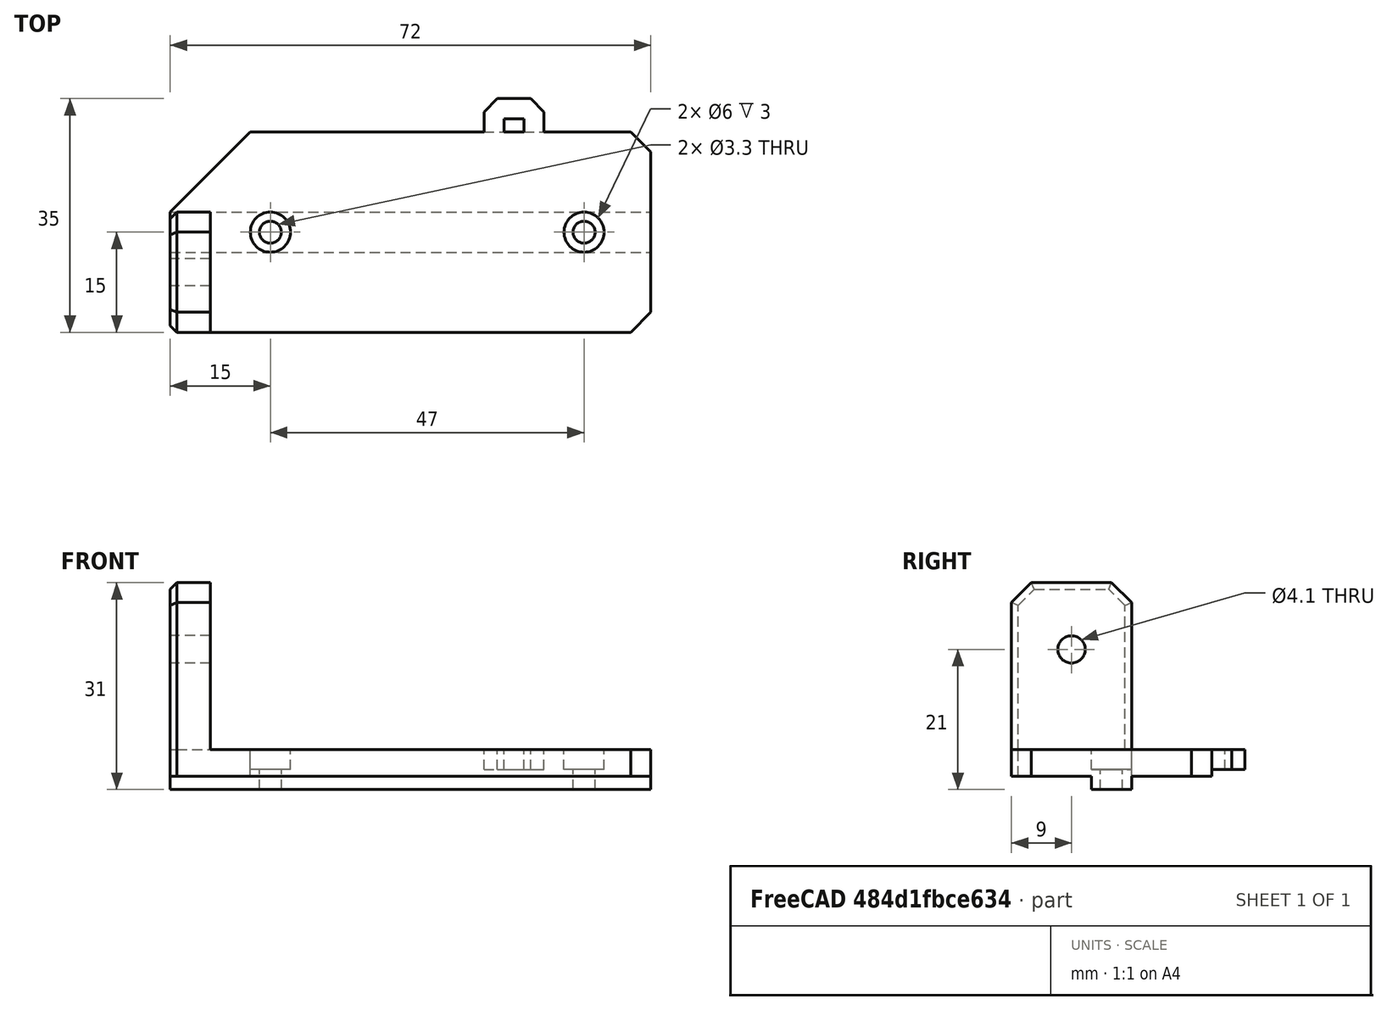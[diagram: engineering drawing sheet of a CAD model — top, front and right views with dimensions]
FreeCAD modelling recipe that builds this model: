
FCSTD DOCUMENT  (FreeCAD 0.18R16146 (Git))
Label: webcam-mounter
License: All rights reserved
LicenseURL: http://en.wikipedia.org/wiki/All_rights_reserved
objects: Part::Chamfer×6, Part::Box×5, Part::Cylinder×5, Part::MultiFuse×4, Part::Cut×4
note: 24 computed .brp shape members not serialized (recipe doc carries the construction recipe); baked Part::Feature solids carry a one-line shape summary decoded from their .brp

FEATURE [Part::Box] Box  label="Cube"
  AttacherType = Attacher::AttachEngine3D
  Height = 25
  Length = 6
  Placement = pos=(0,0,4) rot=(0,0,1;0rad)
  Width = 18
FEATURE [Part::Box] Box001  label="Cube001"
  AttacherType = Attacher::AttachEngine3D
  Height = 4
  Length = 72
  Width = 30
FEATURE [Part::Cylinder] Cylinder
  Angle = 360
  AttacherType = Attacher::AttachEngine3D
  Height = 10
  Placement = pos=(8,9,19) rot=(0,-1,0;1.5708rad)
  Radius = 2.05
FEATURE [Part::Chamfer] Chamfer
  Base = -> Box001
  Edges = 1 edges r=12: [Edge3]
FEATURE [Part::Chamfer] Chamfer001
  Base = -> Chamfer
  Edges = 2 edges r=3: [Edge12,Edge15]
FEATURE [Part::Chamfer] Chamfer002
  Base = -> Box
  Edges = 2 edges r=3: [Edge10,Edge12]
FEATURE [Part::Box] Box002  label="Cube002"
  AttacherType = Attacher::AttachEngine3D
  Height = 2
  Length = 72
  Placement = pos=(0,12,-2) rot=(0,0,1;0rad)
  Width = 6
FEATURE [Part::MultiFuse] Fusion
  Shapes = -> [Box002,Chamfer001]
FEATURE [Part::Cylinder] Cylinder001
  Angle = 360
  AttacherType = Attacher::AttachEngine3D
  Height = 10
  Placement = pos=(15,15,-5) rot=(0,0,1;0rad)
  Radius = 1.65
FEATURE [Part::Cylinder] Cylinder002
  Angle = 360
  AttacherType = Attacher::AttachEngine3D
  Height = 10
  Placement = pos=(62,15,-5) rot=(0,0,1;0rad)
  Radius = 1.65
FEATURE [Part::Cylinder] Cylinder003
  Angle = 360
  AttacherType = Attacher::AttachEngine3D
  Height = 3
  Placement = pos=(62,15,-5) rot=(0,0,1;0rad)
  Radius = 3
FEATURE [Part::Cylinder] Cylinder004
  Angle = 360
  AttacherType = Attacher::AttachEngine3D
  Height = 3
  Placement = pos=(15,15,-5) rot=(0,0,1;0rad)
  Radius = 3
FEATURE [Part::MultiFuse] Fusion001
  Shapes = -> [Cylinder002,Cylinder001]
FEATURE [Part::Cut] Cut001
  Base = -> Fusion
  Tool = -> Fusion001
FEATURE [Part::MultiFuse] Fusion002
  Placement = pos=(0,0,6) rot=(0,0,1;0rad)
  Shapes = -> [Cylinder004,Cylinder003]
FEATURE [Part::Cut] Cut002
  Base = -> Cut001
  Tool = -> Fusion002
FEATURE [Part::Chamfer] Chamfer004
  Base = -> Cut002
  Edges = 1 edges r=1: [Edge10]
FEATURE [Part::Box] Box003  label="Cube003"
  AttacherType = Attacher::AttachEngine3D
  Height = 3
  Length = 9
  Placement = pos=(72,30,0) rot=(0,0,1;0rad)
  Width = 5
FEATURE [Part::Box] Box004  label="Cube004"
  AttacherType = Attacher::AttachEngine3D
  Height = 3
  Length = 3
  Placement = pos=(75,30,0) rot=(0,0,1;0rad)
  Width = 2
FEATURE [Part::Cut] Cut003
  Base = -> Box003
  Placement = pos=(-25,0,1) rot=(0,0,1;0rad)
  Tool = -> Box004
FEATURE [Part::Chamfer] Chamfer005
  Base = -> Cut003
  Edges = 2 edges r=2: [Edge3,Edge15]
FEATURE [Part::Cut] Cut
  Base = -> Chamfer002
  Tool = -> Cylinder
FEATURE [Part::Chamfer] Chamfer006
  Base = -> Cut
  Edges = 5 edges r=1: [Edge1,Edge2,Edge4,Edge5,Edge6]
FEATURE [Part::MultiFuse] Fusion003
  Shapes = -> [Chamfer006,Chamfer004,Chamfer005]
